# Revit family: SoapDispenser_Hob_Nero_Mecca_Sensor
name_source: partatom
category: Specialty Equipment
units: mm (PartAtom-declared; Revit-internal decimal feet)

## family parameters
Always vertical = Yes
Cut with Voids When Loaded = Yes
Maintain Annotation Orientation = No
OmniClass Number = 23.31.25.29.13
OmniClass Title = Hand Soap Dispensers
Part Type = Normal
Room Calculation Point = No
Round Connector Dimension = Use Diameter
Shared = No
Work Plane-Based = No

## types (6) — shared parameters
Assembly Code = C1030220
Default Elevation = 900 mm  [stored 2.95276 ft]
IfcExportAs = IfcFurnitureType
IfcExportType = USERDEFINED
Manufacturer = Nero
ManufacturerOverallDepth = 124 mm  [stored 0.406824 ft]
ManufacturerOverallHeight = 144 mm  [stored 0.472441 ft]
ManufacturerOverallWidth = 45 mm  [stored 0.147638 ft]
ManufacturerURLProductSpecific = https://nerotapware.com.au
ModifiedIssue = 20251105 $
URL = https://nerotapware.com.au
Uniclass2015Code = Pr_40_70_22_81
Uniclass2015Title = Soap dispensers
Uniclass2015Version = Products v1.35

## per-type parameters (varying)
| type | Description | ManufacturerSpecCode | Material | Model | Type Comments |
| Chrome (NR407CH) | Mecca Hob Mounted Sensor Soap Dispensor Chrome | NR407CH | Metal_Chrome_Nero | NR407CH | Soap Dispenser - Hob - Sensor - Chrome |
| Matte Black (NR407MB) | Mecca Hob Mounted Sensor Soap Dispensor Matte Black | NR407MB | Metal_MatteBlack_Nero | NR407MB | Soap Dispenser - Hob - Sensor - Matte Black |
| Brushed Nickel (NR407BN) | Mecca Hob Mounted Sensor Soap Dispensor Brushed Nickel | NR407BN | Metal_Nickel_Nero_Brushed | NR407BN | Soap Dispenser - Hob - Sensor - Brushed Nickel |
| Brushed Gold (NR407BG) | Mecca Hob Mounted Sensor Soap Dispensor Brushed Gold | NR407BG | Metal_Gold_Nero_Brushed | NR407BG | Soap Dispenser - Hob - Sensor - Brushed Gold |
| Brushed Bronze (NR407BZ) | Mecca Hob Mounted Sensor Soap Dispensor Brushed Bronze | NR407BZ | Metal_Bronze_Nero_Brushed | NR407BZ | Soap Dispenser - Hob - Sensor - Brushed Bronze |
| Gunmetal (NR407GM) | Mecca Hob Mounted Sensor Soap Dispensor Gun Metal | NR407GM | Metal_GunMetal_Nero | NR407GM | Soap Dispenser - Hob - Sensor - Gunmetal |

note: [stored X ft] marks values corroborated as IEEE doubles in the binary element streams (Revit-internal decimal feet)

## geometry (parser evidence)
native form markers: Sweep x2
no freeform markers — native parametric forms only
